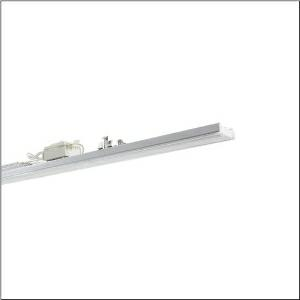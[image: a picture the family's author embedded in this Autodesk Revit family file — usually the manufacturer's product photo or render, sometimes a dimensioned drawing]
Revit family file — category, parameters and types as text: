
# Revit family: licross_21_recessed_mo_52te1edn495g
name_source: partatom
category: Lighting Fixtures
units: mm (PartAtom-declared; Revit-internal decimal feet)

## family parameters
Cut with Voids When Loaded = No
Host = Face
Light Source = No
Part Type = Normal
Room Calculation Point = No
Round Connector Dimension = Use Diameter
Shared = No

## types (1)
- --- (1 x LED, 9940 lm, 58 W, 4000K)
    Apparent Load = 58 VA
    CIE Flux Codes = 85 95 99 100 100
    Color Rendering = 80
    Color Temperature = 4000K
    Default Elevation = 1800 mm
    Description = Licross 21 Recessed MO, luminaire insert, of sheet steel, galvanised, coil coated, white, length: 1.500mm, width: 66mm, height: 67mm, LED rated luminous flux: 9.940lm, light colour: 840, SDCM (Standard Deviation of Colour Matching)MacAdam ≤ 3 SDCM (initial), control gear: DALI 2, with plug, 5-pole, with phase selection, mains connection: 220..240V, AC, 50/60Hz, rated input power: 58W, internal wiring halogen-free, primary light control with lens, of plastic, primary optical cover: cover, of PMMA, light emission: direct distribution, primary light characteristic: symmetric, protection rating (complete): IP54, insulation class (complete): insulation class I (protective earthing), certification: CE, ENEC, VDE, UKCA, protection symbol: D if used in an environment with non-conductive dust loads with corresponding accessories, impact resistance: IK06, permissible ambient temperature for indoor applications: -25..+35°C, corresponds to IFS (International Featured Standards) requirements for safety and quality in the food industry, reducing of maximum allowable ambient temperature of 5°C with ceiling mounting, LABS conformity tested according to VDMA 24364:2018-05, The light source and the operating device comply with the requirements of the Ecodesign Regulation (EU) 2019/2020 and are replaceable in accordance with this regulation, packaging unit: 1 piece
    Height = 58 mm
    Lamp = 1 x LED
    Lamp Light Flux = 9940 lm
    Lamp Power = 58 W
    Lamp count = 1
    Length = 1500 mm
    Luminous efficacy = 171 lm/W
    Manufacturer = Siteco
    ModVariant = No
    Model = 52TE1EDN495G
    Mounting Place = Ceiling
    Mounting Type = Pendant
    Number of Poles = 1
    OnlyDefault = Yes
    Power Factor = 1
    Product Name = Licross 21 Recessed MO
    Product group = luminaire insert | ceiling pendant
    ProductGroupID = 901
    Protection Class = Protection class I
    Protection Degree = IP 54
    RLX_Detail_Level = 1
    RLX_Emergency_Light_Flux = 0 lm
    RLX_Emergency_Type = 0
    RLX_Emergency_Type_DB = No
    RlxData = <blob elided: 24929 chars, md5=542ffbc5>
    Socket = socket
    Standby Power = 0 W
    System Light Flux = 9940 lm
    System Power = 58 W
    Type Comments = factory setting: luminous flux: 100 % | dim-lin: 254 | 390 mA
    Type Image = l_1296930.jpg
    URL = http://relux.com
    VarID = @adj_125179
    Voltage = 0 V
    Weight = 0.00 kg
    Width = 66 mm

## geometry (parser evidence)
native form markers: Blend x4, Sweep x9
no freeform markers — native parametric forms only
